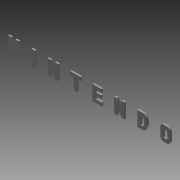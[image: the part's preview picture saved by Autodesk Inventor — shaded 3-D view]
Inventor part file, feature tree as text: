
AUTODESK INVENTOR PART (.ipt)
format: ipt  version: 2012 SP1 (Build 160190100, 190)  size: 184,832 bytes
history: native  units: in
note: dims shown in document units (in); Inventor stores cm internally (conversion verified against a paired STEP export)
features: extrude x3, sketch x3
ambient origin geometry x8: Origin, YZ Plane, XZ Plane, XY Plane, X Axis, Y Axis, Z Axis, Center Point
bodies: Solid1 (feature_tree)
feature tree (6):
  extrude  "Extrusion1"  Depth=0.01in TaperAngle=0.0deg
  extrude  "Extrusion2"  Depth=0.01in TaperAngle=0.0deg
  extrude  "Extrusion3"  [1 undecoded]
  sketch  "Sketch1"  dims[d0=1.0in d1=0.01in d2=0.0in]
  sketch  "Sketch2"  dims[d3=1.0in d4=0.0in]
  sketch  "Sketch3"  dims[d5=0.086in d6=0.069in d7=0.025in d8=0.022in d9=0.01in d10=0.01in d11=0.0in]
note: 1 required parameter value undecoded (feature->parameter linkage not recoverable at this tier; creation-order binding heuristic only, values carry confidence <= 0.55)
